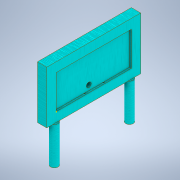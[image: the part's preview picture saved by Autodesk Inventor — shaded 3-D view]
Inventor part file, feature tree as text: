
AUTODESK INVENTOR PART (.ipt)
format: ipt  version: 2021.3 (Build 253353000, 353)  size: 187,904 bytes
history: native  units: mm
features: sketch x9, extrude x6
ambient origin geometry x8: Origin, YZ Plane, XZ Plane, XY Plane, X Axis, Y Axis, Z Axis, Center Point
bodies: Solid1 (feature_tree)
feature tree (15):
  extrude  "Extrusion1"  Depth=10.0mm TaperAngle=0.0deg
  extrude  "Extrusion2"  Depth=36.0mm
  extrude  "Extrusion3"  Depth=10.0mm
  extrude  "Extrusion4"  Depth=10.0mm
  extrude  "Extrusion5"  Depth=2.0mm
  sketch  "Sketch6"  dims[d18=3.0mm d19=20.0mm]
  sketch  "Sketch8"  dims[d20=27.696643mm]
  sketch  "Sketch9"  dims[d21=32.303357mm]
  extrude  "Extrusion7"  Depth=20.0mm
  sketch  "Sketch1"  dims[d4=100.0mm d7=10.0mm d8=0.0mm]
  sketch  "Sketch2"  dims[d9=80.0mm d10=36.0mm]
  sketch  "Sketch3"  dims[d11=10.0mm d12=10.0mm]
  sketch  "Sketch4"  dims[d13=10.0mm d14=10.0mm]
  sketch  "Sketch5"  dims[d15=2.0mm d16=0.0mm d17=3.0mm]
  sketch  "Sketch10"  dims[d22=46.0mm d23=0.0mm d24=0.0mm d25=0.0mm d26=8.0mm d27=8.0mm d28=40.0mm d29=0.0mm d34=80.0mm d35=36.0mm d36=2.0mm d37=0.0mm]
